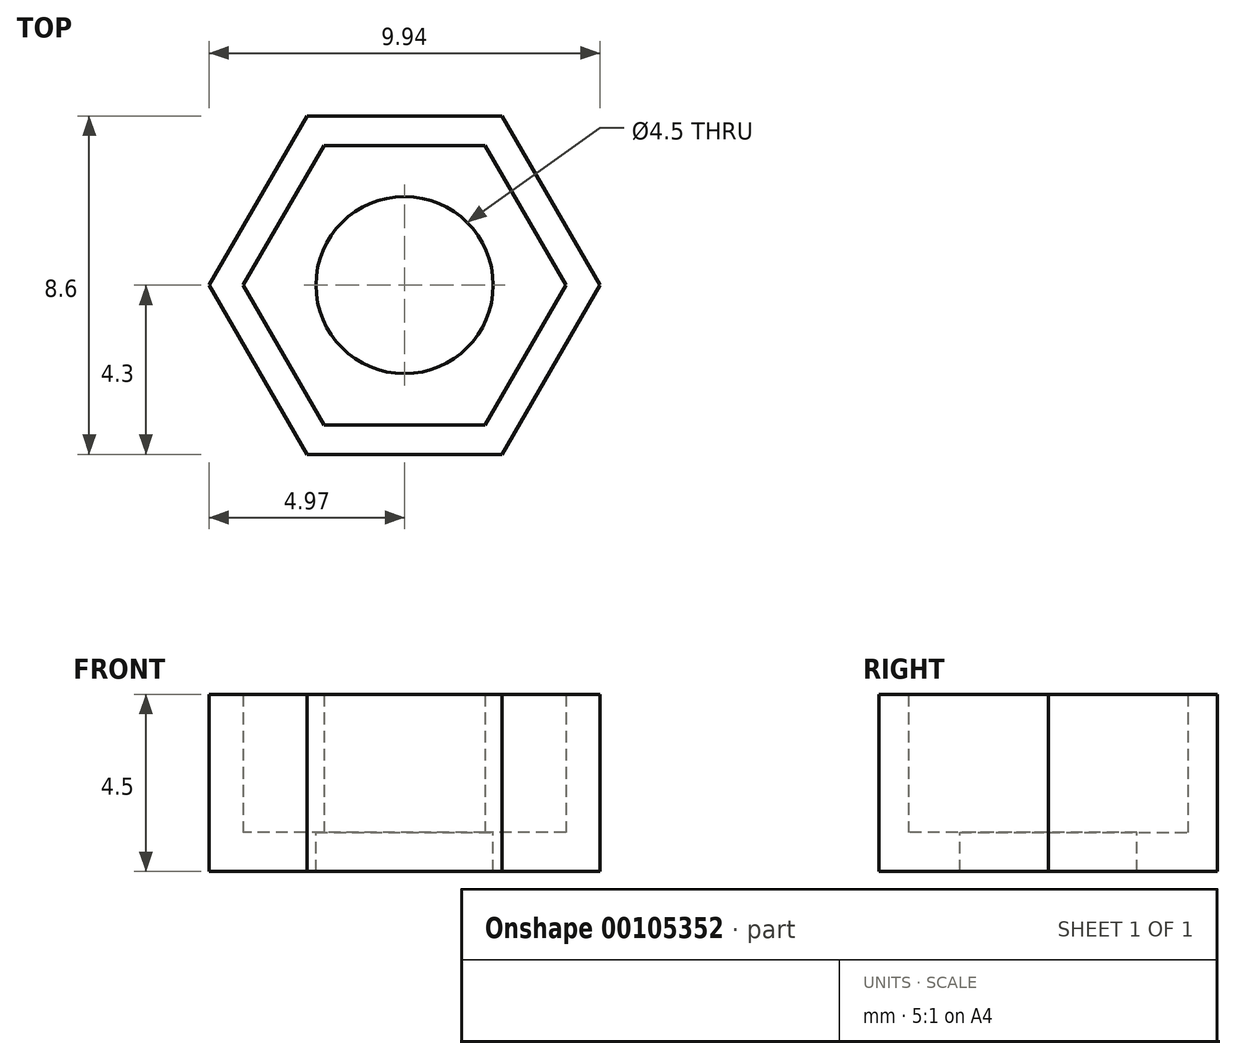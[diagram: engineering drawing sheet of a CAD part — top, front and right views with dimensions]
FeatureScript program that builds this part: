
annotation { "Feature Type Name" : "Feature", "Feature Type Description" : "" }
export const myFeature = defineFeature(function(context is Context, id is Id, definition is map)
    precondition{}
    {
        {
            var Q0;
            Q0=qCreatedBy(makeId("Top.planeOp"),FACE);
            var sketch = newSketch(context, id + "F0", { "sketchPlane" : qUnion([Q0])});
            skCircle(sketch, "E0.cCircle", {"center": v(0, 0) * mm, "radius": 4.3 * mm, "construction": true});
            skLineSegment(sketch, "E0.0", {"start": v(2.48, -4.3) * mm, "end": v(-2.48, -4.3) * mm});
            skLineSegment(sketch, "E0.1", {"start": v(-2.48, -4.3) * mm, "end": v(-4.97, 0) * mm});
            skLineSegment(sketch, "E0.2", {"start": v(-4.97, 0) * mm, "end": v(-2.48, 4.3) * mm});
            skLineSegment(sketch, "E0.3", {"start": v(-2.48, 4.3) * mm, "end": v(2.48, 4.3) * mm});
            skLineSegment(sketch, "E0.4", {"start": v(2.48, 4.3) * mm, "end": v(4.97, 0) * mm});
            skLineSegment(sketch, "E0.5", {"start": v(4.97, 0) * mm, "end": v(2.48, -4.3) * mm});
            skPoint(sketch, "E0.0.midPoint", {"position": v(0, -4.3) * mm});
            skCircle(sketch, "E1.cCircle", {"center": v(0, 0) * mm, "radius": 3.55 * mm, "construction": true});
            skLineSegment(sketch, "E1.0", {"start": v(2.05, -3.55) * mm, "end": v(-2.05, -3.55) * mm});
            skLineSegment(sketch, "E1.1", {"start": v(-2.05, -3.55) * mm, "end": v(-4.1, 0) * mm});
            skLineSegment(sketch, "E1.2", {"start": v(-4.1, 0) * mm, "end": v(-2.05, 3.55) * mm});
            skLineSegment(sketch, "E1.3", {"start": v(-2.05, 3.55) * mm, "end": v(2.05, 3.55) * mm});
            skLineSegment(sketch, "E1.4", {"start": v(2.05, 3.55) * mm, "end": v(4.1, 0) * mm});
            skLineSegment(sketch, "E1.5", {"start": v(4.1, 0) * mm, "end": v(2.05, -3.55) * mm});
            skPoint(sketch, "E1.0.midPoint", {"position": v(0, -3.55) * mm});
            skSolve(sketch);
        }
        {
            var Q0;
            Q0 = qSketchRegion(id + "F0", true);
            extrude(context, id + "F1", {"entities" : qUnion([Q0]), "depth" : 3.5 * mm});
        }
        {
            var Q0;
            Q0=makeQuery(id+"F1.opExtrude","CAP_FACE",FACE,{"disambiguationData":[OSD([sQuery(id+"F0.wireOp",EDGE,"E0.0"),sQuery(id+"F0.wireOp",EDGE,"E0.1"),sQuery(id+"F0.wireOp",EDGE,"E0.2"),sQuery(id+"F0.wireOp",EDGE,"E0.3"),sQuery(id+"F0.wireOp",EDGE,"E0.4"),sQuery(id+"F0.wireOp",EDGE,"E0.5"),sQuery(id+"F0.wireOp",EDGE,"E1.0"),sQuery(id+"F0.wireOp",EDGE,"E1.1"),sQuery(id+"F0.wireOp",EDGE,"E1.2"),sQuery(id+"F0.wireOp",EDGE,"E1.3"),sQuery(id+"F0.wireOp",EDGE,"E1.4"),sQuery(id+"F0.wireOp",EDGE,"E1.5")])],"isStart":true});
            var sketch = newSketch(context, id + "F2", { "sketchPlane" : qUnion([Q0])});
            skLineSegment(sketch, "E2.0", {"start": v(2.48, 4.3) * mm, "end": v(-2.48, 4.3) * mm});
            skLineSegment(sketch, "E3.0", {"start": v(4.97, 0) * mm, "end": v(2.48, 4.3) * mm});
            skLineSegment(sketch, "E4.0", {"start": v(2.48, -4.3) * mm, "end": v(4.97, 0) * mm});
            skLineSegment(sketch, "E5.0", {"start": v(-2.48, -4.3) * mm, "end": v(2.48, -4.3) * mm});
            skLineSegment(sketch, "E6.0", {"start": v(-4.97, 0) * mm, "end": v(-2.48, -4.3) * mm});
            skLineSegment(sketch, "E7.0", {"start": v(-2.48, 4.3) * mm, "end": v(-4.97, 0) * mm});
            skCircle(sketch, "E8", {"center": v(0, 0) * mm, "radius": 2.25 * mm});
            skSolve(sketch);
        }
        {
            var Q0;
            Q0 = qSketchRegion(id + "F2", true);
            extrude(context, id + "F3", {"entities" : qUnion([Q0]), "operationType" : NewBodyOperationType.ADD, "depth" : 1 * mm});
        }
    });
